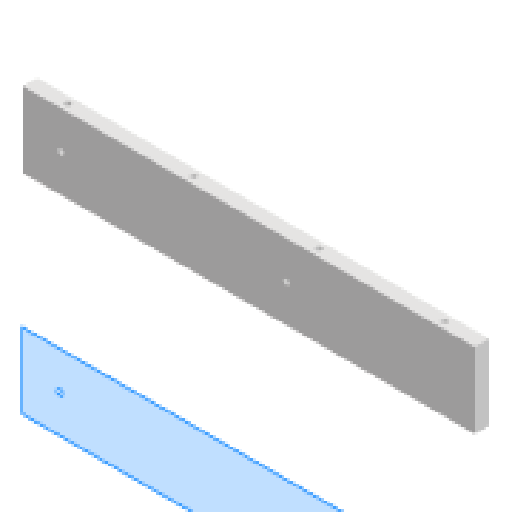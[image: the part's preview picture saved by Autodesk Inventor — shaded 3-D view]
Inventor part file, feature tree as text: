
AUTODESK INVENTOR PART (.ipt)
format: ipt  version: 2024 (Build 280153000, 153)  size: 113,152 bytes
history: native  units: in
note: dims shown in document units (in); Inventor stores cm internally (conversion verified against a paired STEP export)
features: extrude x3, sketch x3
ambient origin geometry x8: Origin, YZ Plane, XZ Plane, XY Plane, X Axis, Y Axis, Z Axis, Center Point
bodies: Solid1 (feature_tree)
feature tree (6):
  extrude  "Extrusion1"  Depth=3.937in
  extrude  "Extrusion2"  Depth=0.748in
  extrude  "Extrusion3"  Depth=0.315in
  sketch  "Sketch1"  dims[d0=23.622in d1=3.937in]
  sketch  "Sketch2"  dims[d2=0.748in d3=0.0in d4=1.9685in]
  sketch  "Sketch3"  dims[d5=9.8425in d6=0.315in d7=0.315in d8=0.4331in d9=0.0in d10=1.9685in d11=6.5617in d12=6.5617in d13=6.5617in d14=1.9685in d15=0.315in d16=0.315in d17=0.315in d18=0.315in d19=0.4331in d20=0.0in]
